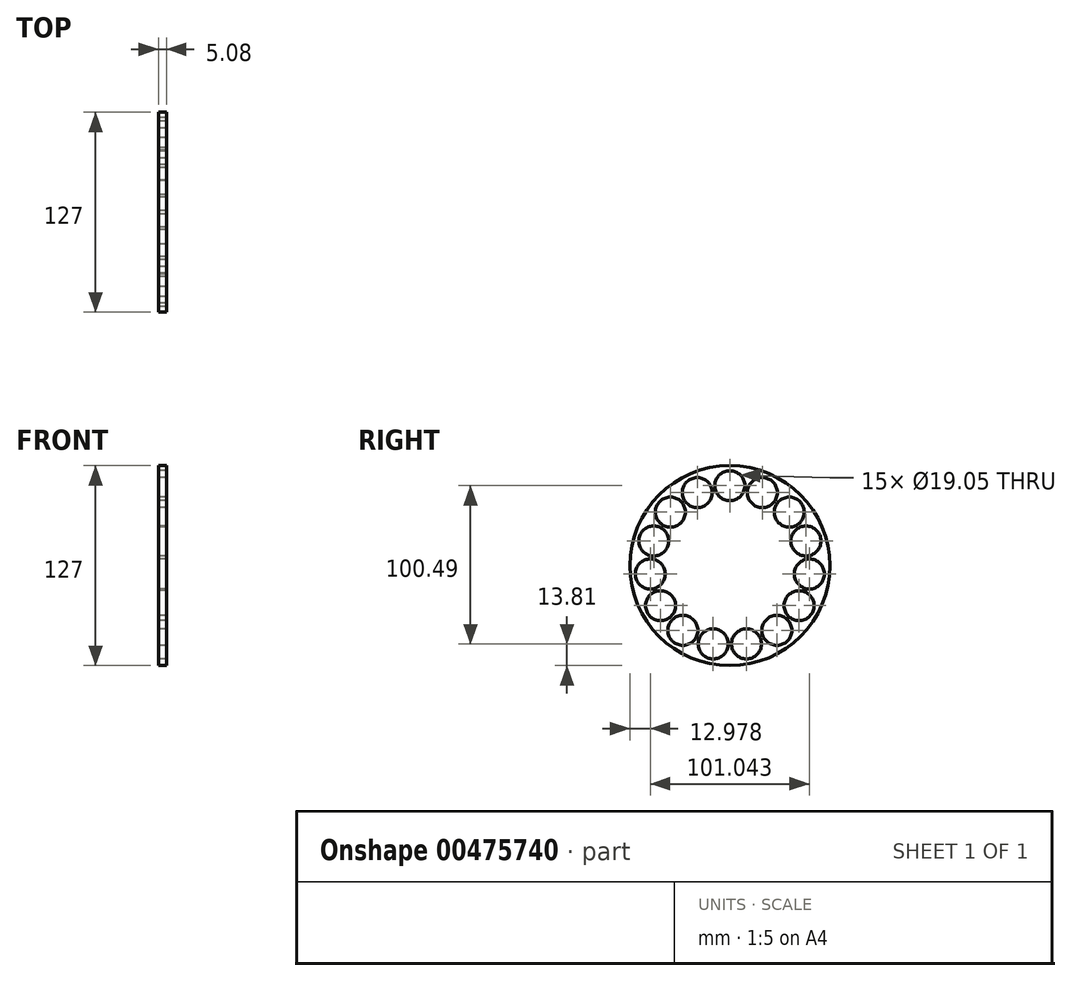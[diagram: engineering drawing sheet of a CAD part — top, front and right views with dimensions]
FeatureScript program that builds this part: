
annotation { "Feature Type Name" : "Feature", "Feature Type Description" : "" }
export const myFeature = defineFeature(function(context is Context, id is Id, definition is map)
    precondition{}
    {
        {
            var Q0;
            Q0=qCreatedBy(makeId("Right.planeOp"),FACE);
            var sketch = newSketch(context, id + "F0", { "sketchPlane" : qUnion([Q0])});
            skCircle(sketch, "E0", {"center": v(0, 0) * mm, "radius": 63.5 * mm});
            skCircle(sketch, "E1", {"center": v(0, 0) * mm, "radius": 50.8 * mm, "construction": true});
            skCircle(sketch, "E2", {"center": v(0, 50.8) * mm, "radius": 9.53 * mm});
            skCircle(sketch, "E3.1.0", {"center": v(-20.66, 46.4) * mm, "radius": 9.53 * mm});
            skCircle(sketch, "E3.2.0", {"center": v(-37.75, 34) * mm, "radius": 9.52 * mm});
            skCircle(sketch, "E3.3.0", {"center": v(-48.31, 15.7) * mm, "radius": 9.53 * mm});
            skCircle(sketch, "E3.4.0", {"center": v(-50.52, -5.31) * mm, "radius": 9.53 * mm});
            skCircle(sketch, "E3.5.0", {"center": v(-44, -25.4) * mm, "radius": 9.53 * mm});
            skCircle(sketch, "E3.6.0", {"center": v(-29.86, -41.1) * mm, "radius": 9.53 * mm});
            skCircle(sketch, "E3.7.0", {"center": v(-10.56, -49.69) * mm, "radius": 9.53 * mm});
            skCircle(sketch, "E3.8.0", {"center": v(10.56, -49.69) * mm, "radius": 9.53 * mm});
            skCircle(sketch, "E3.9.0", {"center": v(29.86, -41.1) * mm, "radius": 9.53 * mm});
            skCircle(sketch, "E3.10.0", {"center": v(44, -25.4) * mm, "radius": 9.53 * mm});
            skCircle(sketch, "E3.11.0", {"center": v(50.52, -5.31) * mm, "radius": 9.53 * mm});
            skCircle(sketch, "E3.12.0", {"center": v(48.31, 15.7) * mm, "radius": 9.53 * mm});
            skCircle(sketch, "E3.13.0", {"center": v(37.75, 34) * mm, "radius": 9.53 * mm});
            skCircle(sketch, "E3.14.0", {"center": v(20.66, 46.4) * mm, "radius": 9.53 * mm});
            skSolve(sketch);
        }
        {
            var Q0;
            Q0 = qSketchRegion(id + "F0", true);
            extrude(context, id + "F1", {"entities" : qUnion([Q0]), "depth" : 5.08 * mm, "offsetDistance" : 25.4 * mm});
        }
    });
